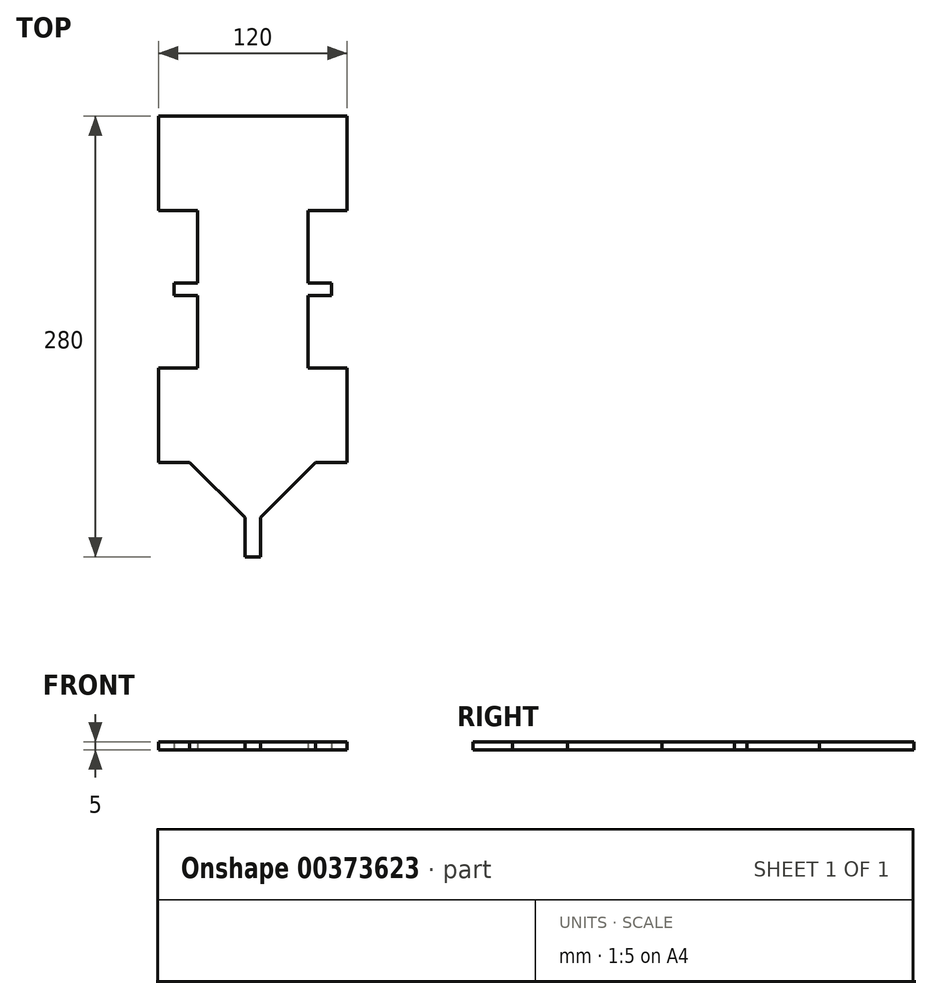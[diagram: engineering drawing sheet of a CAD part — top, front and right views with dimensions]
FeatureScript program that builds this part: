
annotation { "Feature Type Name" : "Feature", "Feature Type Description" : "" }
export const myFeature = defineFeature(function(context is Context, id is Id, definition is map)
    precondition{}
    {
        {
            var Q0;
            Q0=qCreatedBy(makeId("Top.planeOp"),FACE);
            var sketch = newSketch(context, id + "F0", { "sketchPlane" : qUnion([Q0])});
            skLineSegment(sketch, "E0.bottom", {"start": v(60, -110) * mm, "end": v(40, -110) * mm});
            skLineSegment(sketch, "E0.top", {"start": v(60, 110) * mm, "end": v(-60, 110) * mm});
            skLineSegment(sketch, "E0.left", {"start": v(60, -110) * mm, "end": v(60, -50) * mm});
            skLineSegment(sketch, "E0.right", {"start": v(-60, -110) * mm, "end": v(-60, -50) * mm});
            skPoint(sketch, "E0.middle", {"position": v(0, 0) * mm});
            skLineSegment(sketch, "E1", {"start": v(0, 110) * mm, "end": v(0, -110) * mm, "construction": true});
            skLineSegment(sketch, "E2", {"start": v(0, -110) * mm, "end": v(0, -170) * mm, "construction": true});
            skLineSegment(sketch, "E3", {"start": v(-40, -110) * mm, "end": v(-5, -145) * mm});
            skLineSegment(sketch, "E4", {"start": v(-5, -145) * mm, "end": v(-5, -170) * mm});
            skLineSegment(sketch, "E5", {"start": v(-5, -170) * mm, "end": v(5, -170) * mm});
            skLineSegment(sketch, "E6", {"start": v(5, -170) * mm, "end": v(5, -145) * mm});
            skLineSegment(sketch, "E7", {"start": v(5, -145) * mm, "end": v(40, -110) * mm});
            skLineSegment(sketch, "E8.bottom", {"start": v(-35, -50) * mm, "end": v(-60, -50) * mm});
            skLineSegment(sketch, "E8.top", {"start": v(-35, 50) * mm, "end": v(-60, 50) * mm});
            skLineSegment(sketch, "E8.left", {"start": v(-35, -50) * mm, "end": v(-35, -4) * mm});
            skPoint(sketch, "E8.middle", {"position": v(-60, 0) * mm});
            skLineSegment(sketch, "E9.bottom", {"start": v(35, -50) * mm, "end": v(60, -50) * mm});
            skLineSegment(sketch, "E9.top", {"start": v(35, 50) * mm, "end": v(60, 50) * mm});
            skLineSegment(sketch, "E9.left", {"start": v(35, -50) * mm, "end": v(35, -4) * mm});
            skPoint(sketch, "E9.middle", {"position": v(60, 0) * mm});
            skLineSegment(sketch, "E10.trimOffspring", {"start": v(-40, -110) * mm, "end": v(-60, -110) * mm});
            skPoint(sketch, "E11.orphan", {"position": v(-85, -50) * mm});
            skLineSegment(sketch, "E12.trimOffspring", {"start": v(-60, 50) * mm, "end": v(-60, 110) * mm});
            skPoint(sketch, "E13.orphan", {"position": v(-85, 50) * mm});
            skLineSegment(sketch, "E14.trimOffspring", {"start": v(60, 50) * mm, "end": v(60, 110) * mm});
            skPoint(sketch, "E9.right.end.orphan", {"position": v(85, 50) * mm});
            skPoint(sketch, "E15.orphan", {"position": v(85, -50) * mm});
            skLineSegment(sketch, "E16.bottom", {"start": v(-35, -4) * mm, "end": v(-50, -4) * mm});
            skLineSegment(sketch, "E16.top", {"start": v(-35, 4) * mm, "end": v(-50, 4) * mm});
            skLineSegment(sketch, "E16.right", {"start": v(-50, -4) * mm, "end": v(-50, 4) * mm});
            skPoint(sketch, "E16.middle", {"position": v(-42.5, 0) * mm});
            skLineSegment(sketch, "E17.bottom", {"start": v(35, -4) * mm, "end": v(50, -4) * mm});
            skLineSegment(sketch, "E17.top", {"start": v(35, 4) * mm, "end": v(50, 4) * mm});
            skLineSegment(sketch, "E17.right", {"start": v(50, -4) * mm, "end": v(50, 4) * mm});
            skPoint(sketch, "E17.middle", {"position": v(42.5, 0) * mm});
            skLineSegment(sketch, "E18.trimOffspring", {"start": v(-35, 4) * mm, "end": v(-35, 50) * mm});
            skLineSegment(sketch, "E19.trimOffspring", {"start": v(35, 4) * mm, "end": v(35, 50) * mm});
            skLineSegment(sketch, "E20", {"start": v(-50, 0) * mm, "end": v(60, 0) * mm, "construction": true});
            skSolve(sketch);
        }
        {
            var Q0;
            Q0 = qSketchRegion(id + "F0", true);
            extrude(context, id + "F1", {"entities" : qUnion([Q0]), "depth" : 5 * mm});
        }
    });
